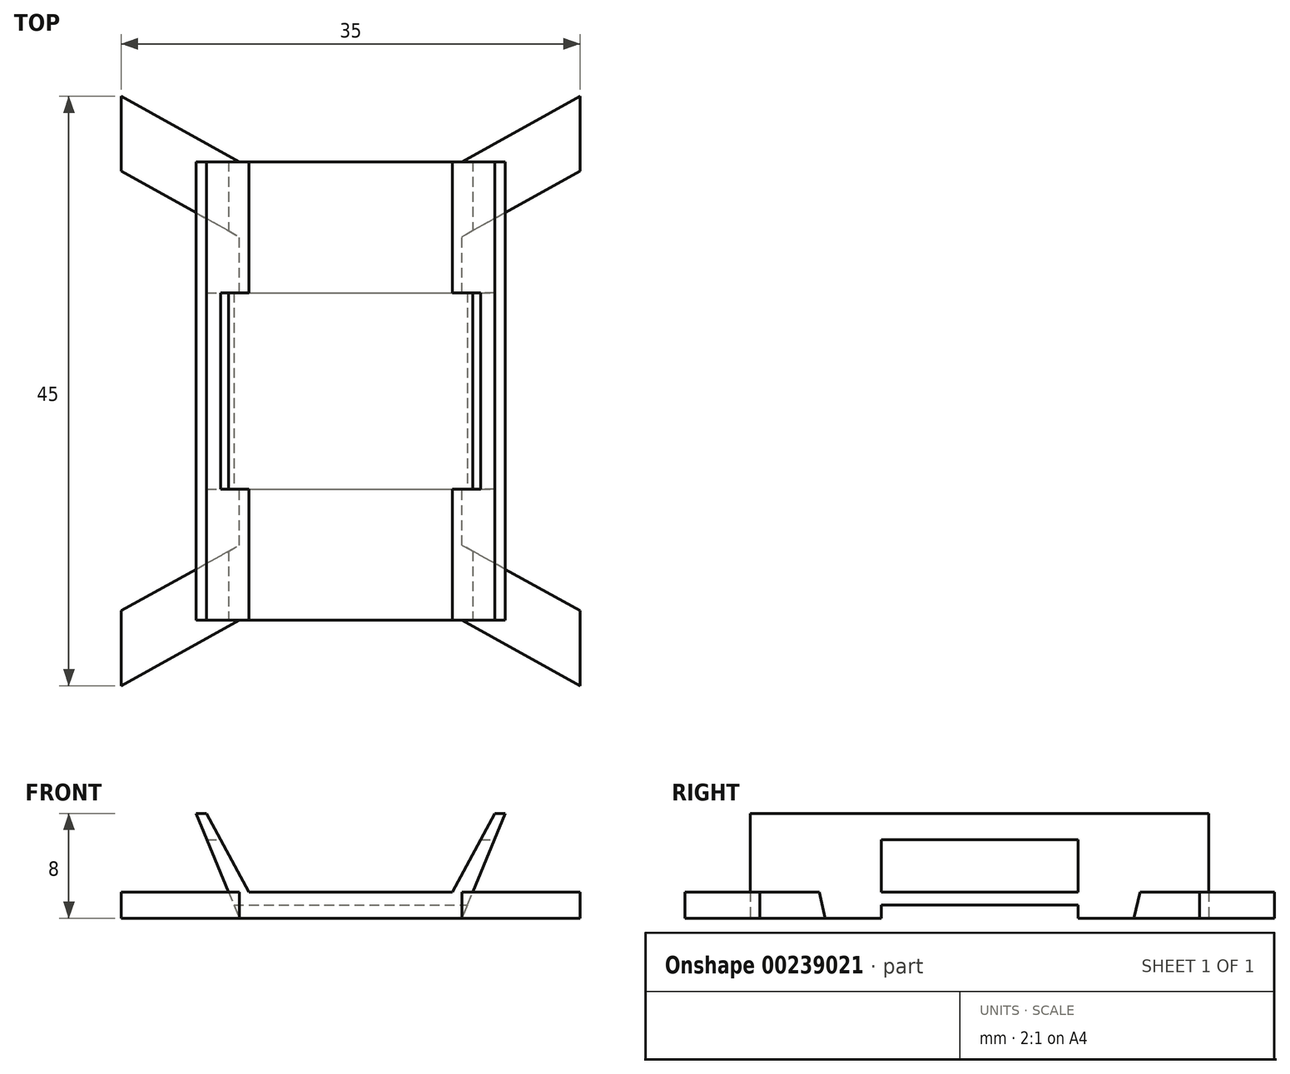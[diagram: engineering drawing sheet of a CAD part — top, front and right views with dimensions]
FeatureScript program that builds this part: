
annotation { "Feature Type Name" : "Feature", "Feature Type Description" : "" }
export const myFeature = defineFeature(function(context is Context, id is Id, definition is map)
    precondition{}
    {
        {
            var Q0;
            Q0=qCreatedBy(makeId("Front.planeOp"),FACE);
            var sketch = newSketch(context, id + "F0", { "sketchPlane" : qUnion([Q0])});
            skLineSegment(sketch, "E0", {"start": v(0, 0) * mm, "end": v(8.5, 0) * mm});
            skLineSegment(sketch, "E1", {"start": v(8.5, 0) * mm, "end": v(11.8, 8) * mm});
            skLineSegment(sketch, "E2", {"start": v(11.8, 8) * mm, "end": v(11, 8) * mm});
            skLineSegment(sketch, "E3", {"start": v(11, 8) * mm, "end": v(7.75, 2) * mm});
            skLineSegment(sketch, "E4", {"start": v(7.75, 2) * mm, "end": v(0, 2) * mm});
            skLineSegment(sketch, "E5.MirrorCS", {"start": v(0, 0) * mm, "end": v(-8.5, 0) * mm});
            skLineSegment(sketch, "E6.MirrorCS", {"start": v(-11.8, 8) * mm, "end": v(-11, 8) * mm});
            skLineSegment(sketch, "E7.MirrorCS", {"start": v(-7.75, 2) * mm, "end": v(0, 2) * mm});
            skLineSegment(sketch, "E8.MirrorCS", {"start": v(-8.5, 0) * mm, "end": v(-11.8, 8) * mm});
            skLineSegment(sketch, "E9.MirrorCS", {"start": v(-11, 8) * mm, "end": v(-7.75, 2) * mm});
            skSolve(sketch);
        }
        {
            var Q0;
            Q0=qSketchRegion(id+"F0",true);
            extrude(context, id + "F1", {"entities" : qUnion([Q0]), "endBound" : BoundingType.SYMMETRIC, "depth" : 35 * mm});
        }
        {
            var Q0;
            Q0=qCreatedBy(makeId("Right.planeOp"),FACE);
            var sketch = newSketch(context, id + "F2", { "sketchPlane" : qUnion([Q0])});
            skLineSegment(sketch, "E10.bottom", {"start": v(7.5, 2) * mm, "end": v(-7.5, 2) * mm});
            skLineSegment(sketch, "E10.top", {"start": v(7.5, 6) * mm, "end": v(-7.5, 6) * mm});
            skLineSegment(sketch, "E10.left", {"start": v(7.5, 2) * mm, "end": v(7.5, 6) * mm});
            skLineSegment(sketch, "E10.right", {"start": v(-7.5, 2) * mm, "end": v(-7.5, 6) * mm});
            skPoint(sketch, "E10.middle", {"position": v(0, 4) * mm});
            skLineSegment(sketch, "E11.bottom", {"start": v(-7.5, 0) * mm, "end": v(7.5, 0) * mm});
            skLineSegment(sketch, "E11.top", {"start": v(-7.5, 1) * mm, "end": v(7.5, 1) * mm});
            skLineSegment(sketch, "E11.left", {"start": v(-7.5, 0) * mm, "end": v(-7.5, 1) * mm});
            skLineSegment(sketch, "E11.right", {"start": v(7.5, 0) * mm, "end": v(7.5, 1) * mm});
            skSolve(sketch);
        }
        {
            var Q0;
            Q0=qSketchRegion(id+"F2",true);
            extrude(context, id + "F3", {"entities" : qUnion([Q0]), "operationType" : NewBodyOperationType.REMOVE, "endBound" : BoundingType.SYMMETRIC, "oppositeDirection" : true, "depth" : 100 * mm});
        }
        {
            var Q0;
            {var subQ1=sQuery(id+"F0.wireOp",EDGE,"E5.MirrorCS");var subQ3=sQuery(id+"F0.wireOp",EDGE,"E0");Q0=makeQuery(id+"F3.boolean.opBoolean","SPLIT",FACE,{"disambiguationData":[TD([makeQuery(id+"F3.opExtrude","SWEPT_FACE",FACE,{"disambiguationData":[OSD([sQuery(id+"F2.wireOp",EDGE,"E11.left")])]})])],"derivedFrom":makeQuery(id+"F1.opExtrude","SWEPT_FACE",FACE,{"disambiguationData":[OSD([subQ3,subQ1])]})});}
            var sketch = newSketch(context, id + "F4", { "sketchPlane" : qUnion([Q0])});
            skLineSegment(sketch, "E12", {"start": v(-8.5, 17.5) * mm, "end": v(-17.5, 22.5) * mm});
            skLineSegment(sketch, "E13", {"start": v(-17.5, 22.5) * mm, "end": v(-17.5, 16.78) * mm});
            skLineSegment(sketch, "E14", {"start": v(-17.5, 16.78) * mm, "end": v(-8.5, 11.78) * mm});
            skLineSegment(sketch, "E15", {"start": v(-8.5, 11.78) * mm, "end": v(-8.5, 17.5) * mm});
            skLineSegment(sketch, "E16.MirrorCS", {"start": v(-17.5, -16.78) * mm, "end": v(-8.5, -11.78) * mm});
            skLineSegment(sketch, "E17.MirrorCS", {"start": v(-8.5, -11.78) * mm, "end": v(-8.5, -17.5) * mm});
            skLineSegment(sketch, "E18.MirrorCS", {"start": v(-17.5, -22.5) * mm, "end": v(-17.5, -16.78) * mm});
            skLineSegment(sketch, "E19.MirrorCS", {"start": v(-8.5, -17.5) * mm, "end": v(-17.5, -22.5) * mm});
            skLineSegment(sketch, "E20.MirrorCS", {"start": v(8.5, -17.5) * mm, "end": v(17.5, -22.5) * mm});
            skLineSegment(sketch, "E21.MirrorCS", {"start": v(17.5, -16.78) * mm, "end": v(8.5, -11.78) * mm});
            skLineSegment(sketch, "E22.MirrorCS", {"start": v(8.5, -11.78) * mm, "end": v(8.5, -17.5) * mm});
            skLineSegment(sketch, "E23.MirrorCS", {"start": v(17.5, -22.5) * mm, "end": v(17.5, -16.78) * mm});
            skLineSegment(sketch, "E24.MirrorCS", {"start": v(8.5, 17.5) * mm, "end": v(17.5, 22.5) * mm});
            skLineSegment(sketch, "E25.MirrorCS", {"start": v(17.5, 16.78) * mm, "end": v(8.5, 11.78) * mm});
            skLineSegment(sketch, "E26.MirrorCS", {"start": v(17.5, 22.5) * mm, "end": v(17.5, 16.78) * mm});
            skLineSegment(sketch, "E27.MirrorCS", {"start": v(8.5, 11.78) * mm, "end": v(8.5, 17.5) * mm});
            skSolve(sketch);
        }
        {
            var Q0;
            Q0 = qSketchRegion(id + "F4", true);
            extrude(context, id + "F5", {"entities" : qUnion([Q0]), "operationType" : NewBodyOperationType.ADD, "oppositeDirection" : true, "depth" : 2 * mm});
        }
    });
